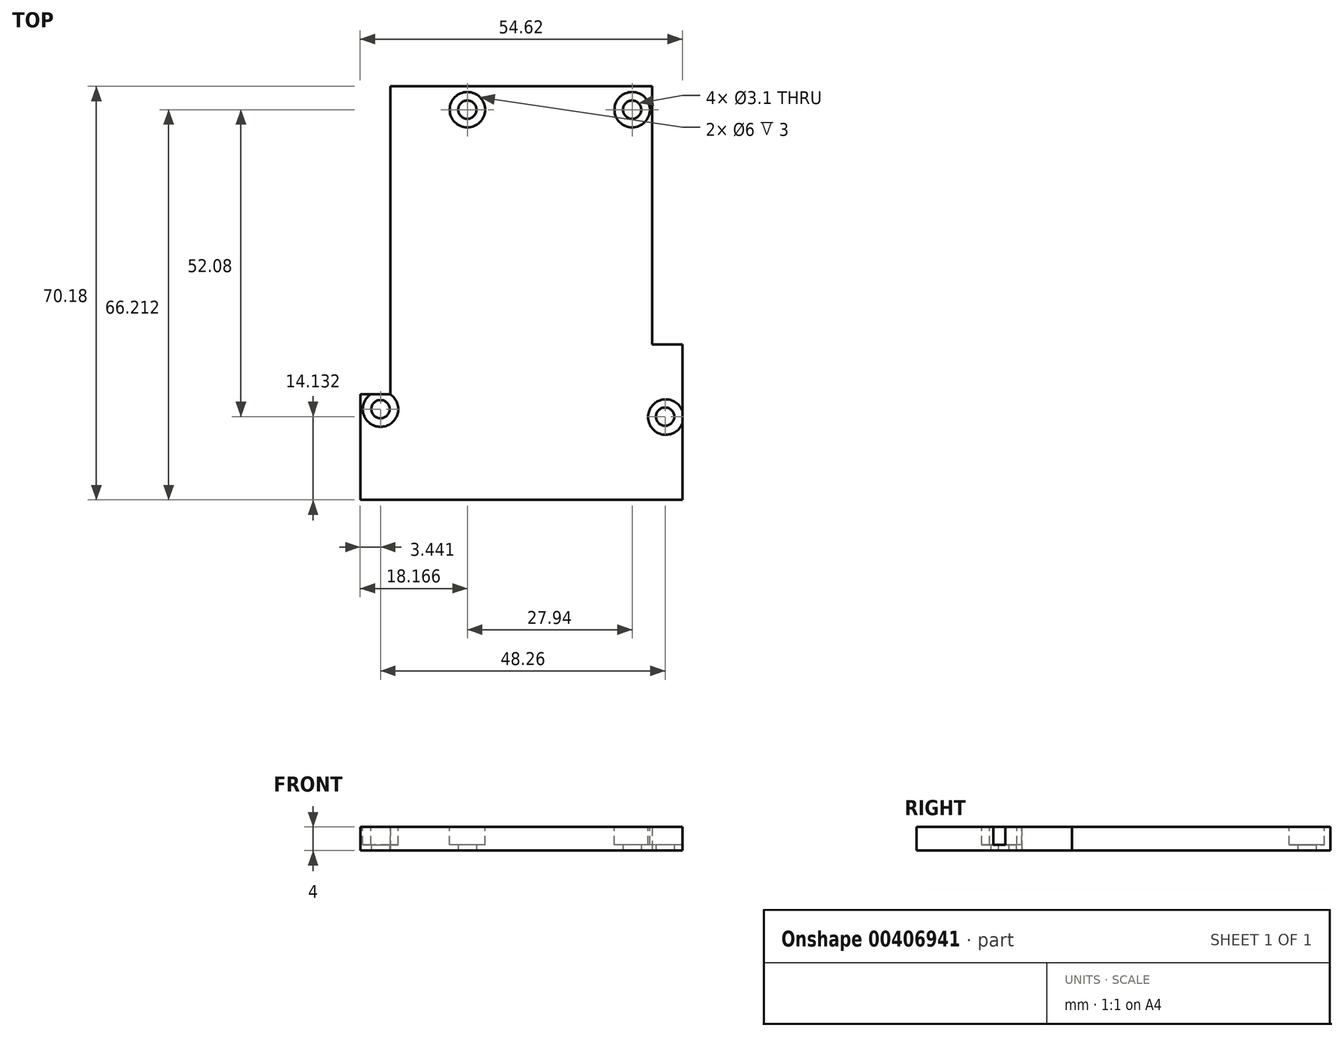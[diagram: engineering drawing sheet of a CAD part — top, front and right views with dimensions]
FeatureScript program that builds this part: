
annotation { "Feature Type Name" : "Feature", "Feature Type Description" : "" }
export const myFeature = defineFeature(function(context is Context, id is Id, definition is map)
    precondition{}
    {
        {
            var Q0;
            Q0=qCreatedBy(makeId("Top.planeOp"),FACE);
            var sketch = newSketch(context, id + "F0", { "sketchPlane" : qUnion([Q0])});
            skLineSegment(sketch, "E0", {"start": v(-19.24, 37.37) * mm, "end": v(25.17, 37.37) * mm});
            skLineSegment(sketch, "E1", {"start": v(25.17, 37.37) * mm, "end": v(25.17, -6.43) * mm});
            skLineSegment(sketch, "E2", {"start": v(25.17, -6.43) * mm, "end": v(30.27, -6.43) * mm});
            skLineSegment(sketch, "E3", {"start": v(30.27, -6.43) * mm, "end": v(30.27, -32.8) * mm});
            skLineSegment(sketch, "E4", {"start": v(30.27, -32.8) * mm, "end": v(-24.35, -32.8) * mm});
            skLineSegment(sketch, "E5", {"start": v(-24.35, -32.8) * mm, "end": v(-24.35, -14.9) * mm});
            skLineSegment(sketch, "E6", {"start": v(-24.35, -14.9) * mm, "end": v(-19.24, -14.9) * mm});
            skLineSegment(sketch, "E7", {"start": v(-19.24, -14.9) * mm, "end": v(-19.24, 37.37) * mm});
            skCircle(sketch, "E8", {"center": v(-6.18, 33.4) * mm, "radius": 1.55 * mm});
            skCircle(sketch, "E9", {"center": v(21.76, 33.4) * mm, "radius": 1.55 * mm});
            skCircle(sketch, "E10", {"center": v(-20.9, -17.4) * mm, "radius": 1.55 * mm});
            skCircle(sketch, "E11", {"center": v(27.35, -18.68) * mm, "radius": 1.55 * mm});
            skSolve(sketch);
        }
        {
            var Q0;
            Q0 = qSketchRegion(id + "F0", true);
            extrude(context, id + "F1", {"entities" : qUnion([Q0]), "depth" : 4 * mm});
        }
        {
            var Q0;
            Q0=makeQuery(id+"F1.opExtrude","CAP_FACE",FACE,{"disambiguationData":[OSD([sQuery(id+"F0.wireOp",EDGE,"E0"),sQuery(id+"F0.wireOp",EDGE,"E1"),sQuery(id+"F0.wireOp",EDGE,"E2"),sQuery(id+"F0.wireOp",EDGE,"E3"),sQuery(id+"F0.wireOp",EDGE,"E4"),sQuery(id+"F0.wireOp",EDGE,"E5"),sQuery(id+"F0.wireOp",EDGE,"E6"),sQuery(id+"F0.wireOp",EDGE,"E7"),sQuery(id+"F0.wireOp",EDGE,"E8"),sQuery(id+"F0.wireOp",EDGE,"E9"),sQuery(id+"F0.wireOp",EDGE,"E10"),sQuery(id+"F0.wireOp",EDGE,"E11")])],"isStart":false});
            var sketch = newSketch(context, id + "F2", { "sketchPlane" : qUnion([Q0])});
            skCircle(sketch, "E12", {"center": v(-20.9, -17.4) * mm, "radius": 3 * mm});
            skCircle(sketch, "E13", {"center": v(27.45, -18.75) * mm, "radius": 3 * mm});
            skCircle(sketch, "E14", {"center": v(-6.18, 33.4) * mm, "radius": 3 * mm});
            skCircle(sketch, "E15", {"center": v(21.76, 33.4) * mm, "radius": 3 * mm});
            skSolve(sketch);
        }
        {
            var Q0;
            Q0 = qSketchRegion(id + "F2", true);
            extrude(context, id + "F3", {"entities" : qUnion([Q0]), "operationType" : NewBodyOperationType.REMOVE, "oppositeDirection" : true, "depth" : 3 * mm});
        }
    });
